# Revit family: Legalett_Linatex_L-Kantelement
name_source: partatom
category: Structural Foundations
units: mm (PartAtom-declared; Revit-internal decimal feet)

## family parameters
Always vertical = Yes
Cap = No
Cut with Voids When Loaded = No
Material for Model Behavior = Other
OmniClass Number = 23.25.05.00
OmniClass Title = Foundations
Shared = No
Show family pre-cut in plan views = Yes
Work Plane-Based = No

## types (4) — shared parameters
Manufacturer = Legalett
Structural Material = Default
Thickness = 100 mm  [stored 0.328084 ft]
Thickness foot = 100 mm  [stored 0.328084 ft]
Width = 500 mm

## per-type parameters (varying)
| type | Foundation Thickness | Model | Type Comments |
| L300 Linatex S200 | 300 mm | Kantelement L300 Linatex S200 | 21200-300 |
| L400 Linatex S200 | 400 mm  [stored 1.31234 ft] | Kantelement L400 Linatex S200 | 21200-400 |
| L450 Linatex S200 | 450 mm | Kantelement L450 Linatex S200 | 21200-450 |
| L500 Linatex S200 | 500 mm | Kantelement L500 Linatex S200 | 21200-500 |

note: [stored X ft] marks values corroborated as IEEE doubles in the binary element streams (Revit-internal decimal feet)

## geometry (parser evidence)
native form markers: Blend x4, Sweep x1
no freeform markers — native parametric forms only
